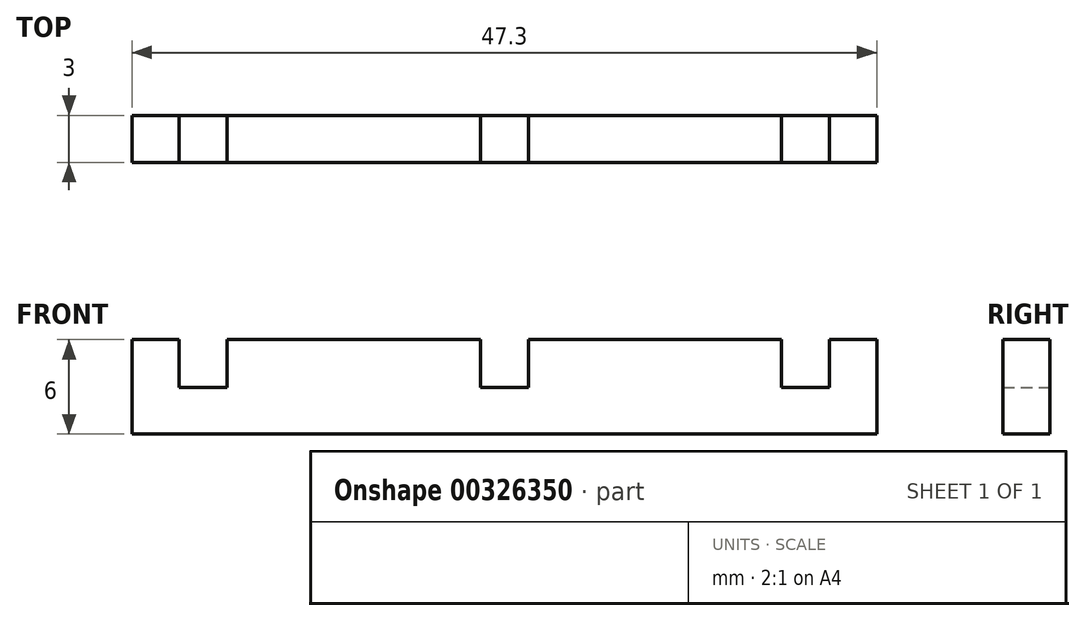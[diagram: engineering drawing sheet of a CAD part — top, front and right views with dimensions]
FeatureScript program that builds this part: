
annotation { "Feature Type Name" : "Feature", "Feature Type Description" : "" }
export const myFeature = defineFeature(function(context is Context, id is Id, definition is map)
    precondition{}
    {
        {
            var Q0;
            Q0=qCreatedBy(makeId("Front.planeOp"),FACE);
            var sketch = newSketch(context, id + "F0", { "sketchPlane" : qUnion([Q0])});
            skLineSegment(sketch, "E0", {"start": v(-23.65, 0) * mm, "end": v(-23.65, 6) * mm});
            skLineSegment(sketch, "E1", {"start": v(-23.65, 6) * mm, "end": v(-20.65, 6) * mm});
            skLineSegment(sketch, "E2", {"start": v(23.65, 6) * mm, "end": v(23.65, 0) * mm});
            skPoint(sketch, "E3", {"position": v(-20.65, 2.98) * mm});
            skPoint(sketch, "E4", {"position": v(-17.6, 2.98) * mm});
            skPoint(sketch, "E5", {"position": v(20.65, 2.98) * mm});
            skPoint(sketch, "E6", {"position": v(17.6, 2.98) * mm});
            skLineSegment(sketch, "E7", {"start": v(-17.6, 2.98) * mm, "end": v(-20.65, 2.98) * mm});
            skLineSegment(sketch, "E8", {"start": v(20.65, 2.98) * mm, "end": v(17.6, 2.98) * mm});
            skLineSegment(sketch, "E9", {"start": v(-23.65, 0) * mm, "end": v(23.65, 0) * mm});
            skLineSegment(sketch, "E10", {"start": v(20.65, 2.98) * mm, "end": v(20.65, 6) * mm});
            skLineSegment(sketch, "E11", {"start": v(17.6, 2.98) * mm, "end": v(17.6, 6) * mm});
            skLineSegment(sketch, "E12", {"start": v(-20.65, 2.98) * mm, "end": v(-20.65, 6) * mm});
            skLineSegment(sketch, "E13", {"start": v(-17.6, 2.98) * mm, "end": v(-17.6, 6) * mm});
            skLineSegment(sketch, "E14.trimOffspring", {"start": v(-17.6, 6) * mm, "end": v(-1.52, 6) * mm});
            skLineSegment(sketch, "E15.trimOffspring", {"start": v(20.65, 6) * mm, "end": v(23.65, 6) * mm});
            skLineSegment(sketch, "E16", {"start": v(-1.52, 6) * mm, "end": v(-1.52, 2.98) * mm});
            skLineSegment(sketch, "E17", {"start": v(-1.52, 2.98) * mm, "end": v(1.52, 2.98) * mm});
            skLineSegment(sketch, "E18", {"start": v(1.52, 2.98) * mm, "end": v(1.52, 6) * mm});
            skLineSegment(sketch, "E19.trimOffspring", {"start": v(1.52, 6) * mm, "end": v(17.6, 6) * mm});
            skSolve(sketch);
        }
        {
            var Q0;
            Q0=makeQuery(id+"F0.imprint","IMPRINT",FACE,{"disambiguationData":[TD([[makeQuery(id+"F0.imprint","IMPRINT",EDGE,{"derivedFrom":sQuery(id+"F0.wireOp",EDGE,"E0")}),-1.0]])]});
            extrude(context, id + "F1", {"entities" : qUnion([Q0]), "depth" : 3 * mm});
        }
    });
